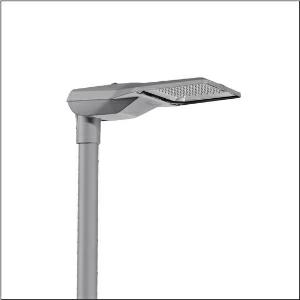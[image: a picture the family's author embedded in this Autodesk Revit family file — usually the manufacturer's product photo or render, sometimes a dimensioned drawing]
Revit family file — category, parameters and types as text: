
# Revit family: streetlight_sl_21_midi___st1_5a_5xe3p43s08lb_fbc0
name_source: partatom
category: Lighting Fixtures
units: mm (PartAtom-declared; Revit-internal decimal feet)

## family parameters
Cut with Voids When Loaded = No
Host = Face
Light Source = No
Part Type = Normal
Room Calculation Point = No
Round Connector Dimension = Use Diameter
Shared = No

## types (1)
- --- (1 x LED, 14690 lm, 98.3 W, 4000K)
    Apparent Load = 98 VA
    CIE Flux Codes = 22 53 95 100 100
    Color Rendering = 70
    Color Temperature = 4000K
    Default Elevation = 1800 mm
    Description = Streetlight SL 21 midi, mast luminaire, primary light control with lens, of PMMA, primary optical cover: cover, of toughened safety glass, transparent, light distribution: ST1.5a, light emission: direct distribution, primary light characteristic: asymmetric, installation type: side-entry, post-top, LED, High Power LED, rated luminous flux: 14.690lm, luminous efficacy: 149lm/W, light colour: 740, colour temperature: 4000K, control: overheat protection, constant luminous flux control, time-dependent luminous flux control, flexible luminous flux parameterisation, presetting dimming logarithmic, mains connection: 230..240V, AC, 50/60Hz, start of lifetime: 98W, end of service life: 101W, reduction: 45W, luminaire housing, of diecast aluminium, powder-coated, Siteco® metallic grey (DB 702S), corrosivity category C5 mid according to DIN EN ISO 12944, please order mast flange separately, inclination adjustable: 0°, 5°, 10°, 15°, sealing non-destructively replaceable, multi-level sealing system, length: 644mm, width: 335mm, height: 110mm, mast flange for spigot size: 42mm (side-entry): 5XC10008XM4, 60/48mm (side-entry/post-top): 5XC10108XM2, 76/60mm (side-entry/post-top): 5XC10108XM1, Smart Interface above, protection rating (complete): IP66, insulation class (complete): insulation class II (safety insulation), certification: CE, ENEC, ENEC+, VDE, impact resistance: IK09, permissible operating ambient temperature for outdoor applications: -40..+50°C, standard-compliant lighting for roads and squares, packaging unit: 1 piece

Light Distribution: ST1.5a
    Height = 111 mm
    Lamp = 1 x LED
    Lamp Light Flux = 14690 lm
    Lamp Power = 98.3 W
    Lamp count = 1
    Length = 644 mm
    Luminous efficacy = 149 lm/W
    Manufacturer = Siteco
    ModVariant = No
    Model = 5XE3P43S08LB
    Number of Poles = 1
    OnlyDefault = Yes
    Power Factor = 1
    Product Name = Streetlight SL 21 midi | ST1.5a
    Product group = mast luminaire | pylon top
    ProductGroupID = 6100
    Protection Class = Protection class II
    Protection Degree = IP 66
    RLX_Detail_Level = 1
    RLX_Emergency_Light_Flux = 0 lm
    RLX_Emergency_Type = 0
    RLX_Emergency_Type_DB = No
    RlxData = <blob elided: 94181 chars, md5=6078bb21>
    Socket = socket
    Standby Power = 0 W
    System Light Flux = 14690 lm
    System Power = 98 W
    Type Comments = factory setting: luminous flux: 100 % | dim-lin: 254 | 1020 mA
    Type Image = l_1004302.jpg
    URL = http://relux.com
    VarID = @adj_127299
    Voltage = 0 V
    Weight = 0.00 kg
    Width = 336 mm

## geometry (parser evidence)
native form markers: Blend x4, Sweep x13
no freeform markers — native parametric forms only
